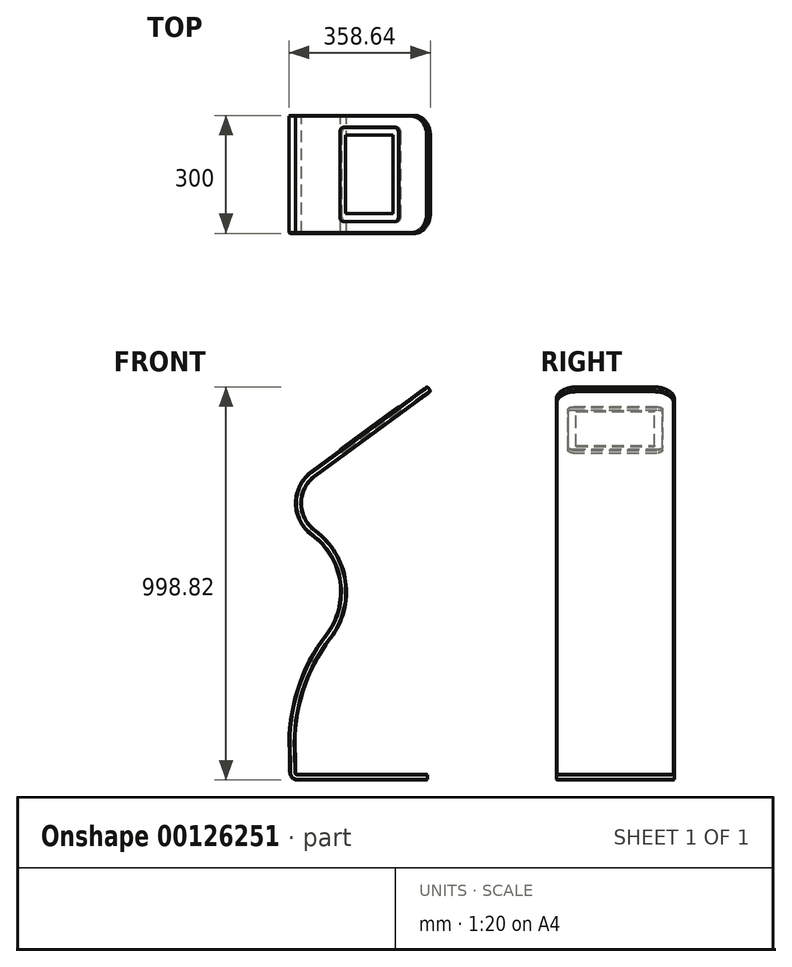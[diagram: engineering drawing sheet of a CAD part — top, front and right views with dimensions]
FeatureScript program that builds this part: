
annotation { "Feature Type Name" : "Feature", "Feature Type Description" : "" }
export const myFeature = defineFeature(function(context is Context, id is Id, definition is map)
    precondition{}
    {
        {
            var Q0;
            Q0=qCreatedBy(makeId("Front.planeOp"),FACE);
            var sketch = newSketch(context, id + "F0", { "sketchPlane" : qUnion([Q0])});
            skLineSegment(sketch, "E0.bottom", {"start": v(20, 0) * mm, "end": v(349.28, 0) * mm});
            skPoint(sketch, "E1.visualSharp", {"position": v(0, 0) * mm});
            skArc(sketch, "E1.filletArc", {"start": v(0, 20) * mm, "mid": v(5.86, 5.86) * mm, "end": v(20, 0) * mm});
            skLineSegment(sketch, "E2", {"start": v(349.28, 1000) * mm, "end": v(56.22, 785.06) * mm});
            skArc(sketch, "E3", {"start": v(56.22, 785.06) * mm, "mid": v(14.91, 703.54) * mm, "end": v(56.22, 622.02) * mm});
            skArc(sketch, "E4", {"start": v(-1.2, 73.24) * mm, "mid": v(19.24, 229.46) * mm, "end": v(92.1, 369.17) * mm});
            skArc(sketch, "E5", {"start": v(92.1, 369.17) * mm, "mid": v(127.4, 503.15) * mm, "end": v(56.22, 622.02) * mm});
            skArc(sketch, "E6", {"start": v(-1.2, 73.24) * mm, "mid": v(-0.3, 46.62) * mm, "end": v(0, 20) * mm});
            skPoint(sketch, "E7.orphan", {"position": v(0, 132.4) * mm});
            skLineSegment(sketch, "E8", {"start": v(349.28, 0) * mm, "end": v(349.28, 15) * mm});
            skLineSegment(sketch, "E9.0", {"start": v(20, 15) * mm, "end": v(349.28, 15) * mm});
            skArc(sketch, "E9.1", {"start": v(15, 20) * mm, "mid": v(16.46, 16.46) * mm, "end": v(20, 15) * mm});
            skArc(sketch, "E9.2", {"start": v(13.78, 73.91) * mm, "mid": v(14.7, 46.96) * mm, "end": v(15, 20) * mm});
            skLineSegment(sketch, "E9.3", {"start": v(358.15, 987.9) * mm, "end": v(65.1, 772.96) * mm});
            skArc(sketch, "E9.4", {"start": v(65.1, 772.96) * mm, "mid": v(29.91, 703.54) * mm, "end": v(65.1, 634.11) * mm});
            skArc(sketch, "E9.5", {"start": v(103.99, 360.02) * mm, "mid": v(142.24, 505.25) * mm, "end": v(65.1, 634.11) * mm});
            skArc(sketch, "E9.6", {"start": v(13.78, 73.91) * mm, "mid": v(33.54, 224.95) * mm, "end": v(103.99, 360.02) * mm});
            skLineSegment(sketch, "E10", {"start": v(349.28, 1000) * mm, "end": v(358.15, 987.9) * mm});
            skSolve(sketch);
        }
        {
            var Q0;
            Q0=makeQuery(id+"F0.imprint","IMPRINT",FACE,{"disambiguationData":[TD([[makeQuery(id+"F0.imprint","IMPRINT",EDGE,{"derivedFrom":sQuery(id+"F0.wireOp",EDGE,"E0.bottom")}),1.0]])]});
            extrude(context, id + "F1", {"entities" : qUnion([Q0]), "depth" : 300 * mm, "offsetDistance" : 25 * mm, "symmetric" : true});
        }
        {
            var Q0;
            Q0=makeQuery(id+"F1.opExtrude","SWEPT_FACE",FACE,{"disambiguationData":[OSD([sQuery(id+"F0.wireOp",EDGE,"E2")])]});
            var sketch = newSketch(context, id + "F2", { "sketchPlane" : qUnion([Q0])});
            skLineSegment(sketch, "E11.bottom", {"start": v(598.85, -108) * mm, "end": v(598.85, 108) * mm});
            skLineSegment(sketch, "E11.top", {"start": v(783.85, -108) * mm, "end": v(783.85, 108) * mm});
            skLineSegment(sketch, "E11.left", {"start": v(610.85, -120) * mm, "end": v(771.85, -120) * mm});
            skLineSegment(sketch, "E11.right", {"start": v(610.85, 120) * mm, "end": v(771.85, 120) * mm});
            skPoint(sketch, "E11.middle", {"position": v(691.35, 0) * mm});
            skLineSegment(sketch, "E12.bottom", {"start": v(616.35, -100) * mm, "end": v(616.35, 100) * mm});
            skLineSegment(sketch, "E12.top", {"start": v(766.35, -100) * mm, "end": v(766.35, 100) * mm});
            skLineSegment(sketch, "E12.left", {"start": v(616.35, -100) * mm, "end": v(766.35, -100) * mm});
            skLineSegment(sketch, "E12.right", {"start": v(616.35, 100) * mm, "end": v(766.35, 100) * mm});
            skPoint(sketch, "E13.orphan", {"position": v(691.35, 181.72) * mm});
            skPoint(sketch, "E14.orphan", {"position": v(841.35, 0) * mm});
            skPoint(sketch, "E15.orphan", {"position": v(691.35, -181.72) * mm});
            skPoint(sketch, "E16.visualSharp", {"position": v(783.85, 120) * mm});
            skArc(sketch, "E16.filletArc", {"start": v(783.85, 108) * mm, "mid": v(780.33, 116.49) * mm, "end": v(771.85, 120) * mm});
            skPoint(sketch, "E17.visualSharp", {"position": v(598.85, 120) * mm});
            skArc(sketch, "E17.filletArc", {"start": v(610.85, 120) * mm, "mid": v(602.36, 116.49) * mm, "end": v(598.85, 108) * mm});
            skPoint(sketch, "E18.visualSharp", {"position": v(598.85, -120) * mm});
            skArc(sketch, "E18.filletArc", {"start": v(598.85, -108) * mm, "mid": v(602.36, -116.49) * mm, "end": v(610.85, -120) * mm});
            skPoint(sketch, "E19.visualSharp", {"position": v(783.85, -120) * mm});
            skArc(sketch, "E19.filletArc", {"start": v(771.85, -120) * mm, "mid": v(780.33, -116.49) * mm, "end": v(783.85, -108) * mm});
            skSolve(sketch);
        }
        {
            var Q0;
            Q0=makeQuery(id+"F2.imprint","IMPRINT",FACE,{"disambiguationData":[TD([[makeQuery(id+"F2.imprint","IMPRINT",EDGE,{"derivedFrom":sQuery(id+"F2.wireOp",EDGE,"E11.bottom")}),-1.0]])]});
            var Q1;
            Q1=makeQuery(id+"F2.imprint","IMPRINT",FACE,{"disambiguationData":[TD([[makeQuery(id+"F2.imprint","IMPRINT",EDGE,{"derivedFrom":sQuery(id+"F2.wireOp",EDGE,"E12.bottom")}),-1.0]])]});
            extrude(context, id + "F3", {"entities" : qUnion([Q0, Q1]), "operationType" : NewBodyOperationType.REMOVE, "oppositeDirection" : true, "depth" : 8 * mm, "offsetDistance" : 25 * mm});
        }
        {
            var Q0;
            Q0=makeQuery(id+"F2.imprint","IMPRINT",FACE,{"disambiguationData":[TD([[makeQuery(id+"F2.imprint","IMPRINT",EDGE,{"derivedFrom":sQuery(id+"F2.wireOp",EDGE,"E11.bottom")}),-1.0]])]});
            extrude(context, id + "F4", {"entities" : qUnion([Q0]), "depth" : 2 * mm, "offsetDistance" : 25 * mm});
        }
        {
            var Q0;
            Q0=makeQuery(id+"F2.imprint","IMPRINT",FACE,{"disambiguationData":[TD([[makeQuery(id+"F2.imprint","IMPRINT",EDGE,{"derivedFrom":sQuery(id+"F2.wireOp",EDGE,"E12.bottom")}),-1.0]])]});
            extrude(context, id + "F5", {"entities" : qUnion([Q0]), "depth" : 2 * mm, "offsetDistance" : 25 * mm});
        }
        {
            var Q0;
            Q0=makeQuery(id+"F4.opExtrude","CAP_EDGE",EDGE,{"disambiguationData":[OSD([sQuery(id+"F2.wireOp",EDGE,"E11.left")])],"isStart":false});
            chamfer(context, id + "F6", {"entities" : qUnion([Q0]), "width" : 0.5 * mm, "tangentPropagation" : true});
        }
        {
            var Q0;
            Q0=makeQuery(id+"F1.opExtrude","CAP_EDGE",EDGE,{"disambiguationData":[OSD([sQuery(id+"F0.wireOp",EDGE,"E10")])],"isStart":false});
            var Q1;
            Q1=makeQuery(id+"F1.opExtrude","CAP_EDGE",EDGE,{"disambiguationData":[OSD([sQuery(id+"F0.wireOp",EDGE,"E10")])],"isStart":true});
            var Q2;
            Q2=makeQuery(id+"F1.opExtrude","CAP_EDGE",EDGE,{"disambiguationData":[OSD([sQuery(id+"F0.wireOp",EDGE,"E8")])],"isStart":false});
            var Q3;
            Q3=makeQuery(id+"F1.opExtrude","CAP_EDGE",EDGE,{"disambiguationData":[OSD([sQuery(id+"F0.wireOp",EDGE,"E8")])],"isStart":true});
            fillet(context, id + "F7", {"entities" : qUnion([Q0, Q1, Q2, Q3]), "tangentPropagation" : true, "radius" : 50 * mm, "defaultsChanged" : true, "vertexSettings" : [], "allowEdgeOverflow" : false});
        }
        {
            var Q0;
            Q0=makeQuery(id+"F1.opExtrude","SWEPT_EDGE",EDGE,{"disambiguationData":[OSD([sQuery(id+"F0.wireOp",EDGE,"E2"),sQuery(id+"F0.wireOp",EDGE,"E10")])]});
            var Q1;
            Q1=makeQuery(id+"F3.boolean.opBoolean","COPY",EDGE,{"derivedFrom":makeQuery(id+"F3.opExtrude","CAP_EDGE",EDGE,{"disambiguationData":[OSD([sQuery(id+"F2.wireOp",EDGE,"E11.left")])],"isStart":true})});
            var Q2;
            Q2=makeQuery(id+"F1.opExtrude","SWEPT_EDGE",EDGE,{"disambiguationData":[OSD([sQuery(id+"F0.wireOp",EDGE,"E9.3"),sQuery(id+"F0.wireOp",EDGE,"E10")])]});
            chamfer(context, id + "F8", {"entities" : qUnion([Q0, Q1, Q2]), "width" : 2 * mm, "tangentPropagation" : true});
        }
    });
